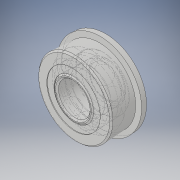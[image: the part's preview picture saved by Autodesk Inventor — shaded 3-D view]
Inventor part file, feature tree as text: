
AUTODESK INVENTOR PART (.ipt)
format: ipt  version: 2019 (Build 230136000, 136)  size: 560,128 bytes
history: native  units: in
note: dims shown in document units (in); Inventor stores cm internally (conversion verified against a paired STEP export)
features: other x9, revolve x5
ambient origin geometry x8: Origin, YZ Plane, XZ Plane, XY Plane, X Axis, Y Axis, Z Axis, Center Point
bodies: Solid1 (feature_tree), Solid2 (feature_tree), Solid3 (feature_tree), Solid4 (feature_tree), Solid5 (feature_tree), Solid6 (feature_tree), Solid7 (feature_tree), Solid8 (feature_tree), Solid9 (feature_tree), Solid10 (feature_tree), Solid11 (feature_tree), Solid12 (feature_tree), Solid13 (feature_tree), Solid14 (feature_tree)
feature tree (14):
  revolve  "Revolve3"  [1 undecoded]
  revolve  "Revolve4"  [1 undecoded]
  other  "CirPattern1[1]"
  other  "CirPattern1[2]"
  other  "CirPattern1[3]"
  other  "CirPattern1[4]"
  other  "CirPattern1[5]"
  other  "CirPattern1[6]"
  other  "CirPattern1[7]"
  other  "CirPattern1[8]"
  other  "CirPattern1[9]"
  revolve  "Revolve5[1]"  [1 undecoded]
  revolve  "Revolve5[2]"  [1 undecoded]
  revolve  "Revolve6"  [1 undecoded]
note: 5 required parameter values undecoded (feature->parameter linkage not recoverable at this tier; creation-order binding heuristic only, values carry confidence <= 0.55)
